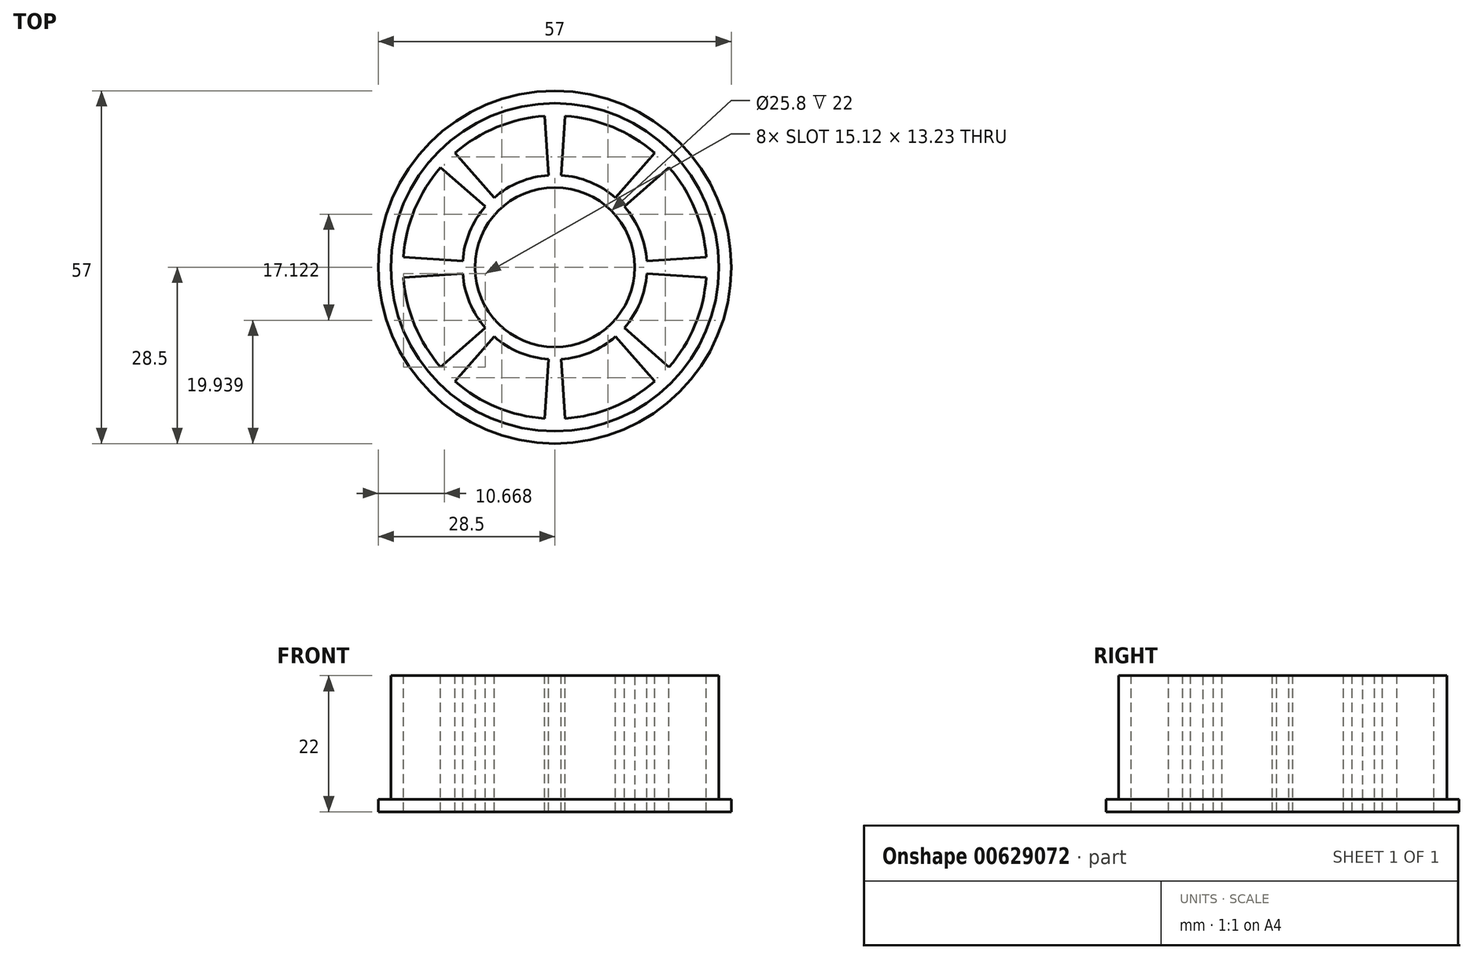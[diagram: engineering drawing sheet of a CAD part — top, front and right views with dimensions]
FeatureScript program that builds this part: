
annotation { "Feature Type Name" : "Feature", "Feature Type Description" : "" }
export const myFeature = defineFeature(function(context is Context, id is Id, definition is map)
    precondition{}
    {
        {
            var Q0;
            Q0=qCreatedBy(makeId("Top.planeOp"),FACE);
            var sketch = newSketch(context, id + "F0", { "sketchPlane" : qUnion([Q0])});
            skCircle(sketch, "E0", {"center": v(0, 0) * mm, "radius": 28.5 * mm});
            skCircle(sketch, "E1", {"center": v(0, 0) * mm, "radius": 26.5 * mm});
            skCircle(sketch, "E2", {"center": v(0, 0) * mm, "radius": 12.9 * mm});
            skSolve(sketch);
        }
        {
            var Q0;
            Q0=makeQuery(id+"F0.imprint","IMPRINT",FACE,{"disambiguationData":[TD([[makeQuery(id+"F0.imprint","IMPRINT",EDGE,{"derivedFrom":sQuery(id+"F0.wireOp",EDGE,"E1")}),1.0]])]});
            extrude(context, id + "F1", {"entities" : qUnion([Q0]), "depth" : 22 * mm, "offsetDistance" : 25 * mm});
        }
        {
            var Q0;
            Q0=makeQuery(id+"F0.imprint","IMPRINT",FACE,{"disambiguationData":[TD([[makeQuery(id+"F0.imprint","IMPRINT",EDGE,{"derivedFrom":sQuery(id+"F0.wireOp",EDGE,"E0")}),1.0]])]});
            extrude(context, id + "F2", {"entities" : qUnion([Q0]), "operationType" : NewBodyOperationType.ADD, "depth" : 2 * mm, "offsetDistance" : 25 * mm});
        }
        {
            var Q0;
            Q0=makeQuery(id+"F1.opExtrude","CAP_FACE",FACE,{"disambiguationData":[OSD([sQuery(id+"F0.wireOp",EDGE,"E1"),sQuery(id+"F0.wireOp",EDGE,"E2")])],"isStart":false});
            var sketch = newSketch(context, id + "F3", { "sketchPlane" : qUnion([Q0])});
            skLineSegment(sketch, "E3", {"start": v(16.12, -18.45) * mm, "end": v(9.8, -11.22) * mm});
            skLineSegment(sketch, "E4", {"start": v(1.64, -24.44) * mm, "end": v(1, -14.87) * mm});
            skArc(sketch, "E5", {"start": v(1, -14.87) * mm, "mid": v(5.7, -13.77) * mm, "end": v(9.8, -11.22) * mm});
            skArc(sketch, "E6", {"start": v(1.64, -24.44) * mm, "mid": v(9.38, -22.64) * mm, "end": v(16.12, -18.45) * mm});
            skLineSegment(sketch, "E7", {"start": v(18.74, -18.74) * mm, "end": v(0, 0) * mm, "construction": true});
            skSolve(sketch);
        }
        {
            var Q0;
            Q0 = qSketchRegion(id + "F3", true);
            var Q1;
            {var subQ0=sQuery(id+"F0.wireOp",EDGE,"E1");Q1=makeQuery(id+"F2.boolean.opBoolean","MERGE",FACE,{"derivedFrom":[makeQuery(id+"F1.opExtrude","CAP_FACE",FACE,{"disambiguationData":[OSD([subQ0,sQuery(id+"F0.wireOp",EDGE,"E2")])],"isStart":true}),makeQuery(id+"F2.opExtrude","CAP_FACE",FACE,{"disambiguationData":[OSD([sQuery(id+"F0.wireOp",EDGE,"E0"),subQ0])],"isStart":true})]});}
            extrude(context, id + "F4", {"entities" : qUnion([Q0]), "endBound" : BoundingType.UP_TO_SURFACE, "oppositeDirection" : true, "depth" : 25 * mm, "endBoundEntityFace" : qUnion([Q1]), "offsetDistance" : 25 * mm});
        }
        {
            var Q0;
            Q0=makeQuery(id+"F4.opExtrude","SWEPT_BODY",BODY,{"disambiguationData":[OSD([sQuery(id+"F3.wireOp",EDGE,"E3"),sQuery(id+"F3.wireOp",EDGE,"E4"),sQuery(id+"F3.wireOp",EDGE,"E5"),sQuery(id+"F3.wireOp",EDGE,"E6")])]});
            var Q1;
            Q1=makeQuery(id+"F1.opExtrude","SWEPT_FACE",FACE,{"disambiguationData":[OSD([sQuery(id+"F0.wireOp",EDGE,"E2")])]});
            circularPattern(context, id + "F5", {"entities" : qUnion([Q0]), "axis" : qUnion([Q1]), "angle" : 360 * degree, "instanceCount" : 8, "equalSpace" : true});
        }
        {
            var Q0;
            Q0=makeQuery(id+"F4.opExtrude","SWEPT_BODY",BODY,{"disambiguationData":[OSD([sQuery(id+"F3.wireOp",EDGE,"E3"),sQuery(id+"F3.wireOp",EDGE,"E4"),sQuery(id+"F3.wireOp",EDGE,"E5"),sQuery(id+"F3.wireOp",EDGE,"E6")])]});
            var Q1;
            Q1=makeQuery(id+"F5.opPattern","COPY",BODY,{"derivedFrom":makeQuery(id+"F4.opExtrude","SWEPT_BODY",BODY,{"disambiguationData":[OSD([sQuery(id+"F3.wireOp",EDGE,"E3"),sQuery(id+"F3.wireOp",EDGE,"E4"),sQuery(id+"F3.wireOp",EDGE,"E5"),sQuery(id+"F3.wireOp",EDGE,"E6")])]}),"instanceName":"7"});
            var Q2;
            Q2=makeQuery(id+"F5.opPattern","COPY",BODY,{"derivedFrom":makeQuery(id+"F4.opExtrude","SWEPT_BODY",BODY,{"disambiguationData":[OSD([sQuery(id+"F3.wireOp",EDGE,"E3"),sQuery(id+"F3.wireOp",EDGE,"E4"),sQuery(id+"F3.wireOp",EDGE,"E5"),sQuery(id+"F3.wireOp",EDGE,"E6")])]}),"instanceName":"6"});
            var Q3;
            Q3=makeQuery(id+"F5.opPattern","COPY",BODY,{"derivedFrom":makeQuery(id+"F4.opExtrude","SWEPT_BODY",BODY,{"disambiguationData":[OSD([sQuery(id+"F3.wireOp",EDGE,"E3"),sQuery(id+"F3.wireOp",EDGE,"E4"),sQuery(id+"F3.wireOp",EDGE,"E5"),sQuery(id+"F3.wireOp",EDGE,"E6")])]}),"instanceName":"5"});
            var Q4;
            Q4=makeQuery(id+"F5.opPattern","COPY",BODY,{"derivedFrom":makeQuery(id+"F4.opExtrude","SWEPT_BODY",BODY,{"disambiguationData":[OSD([sQuery(id+"F3.wireOp",EDGE,"E3"),sQuery(id+"F3.wireOp",EDGE,"E4"),sQuery(id+"F3.wireOp",EDGE,"E5"),sQuery(id+"F3.wireOp",EDGE,"E6")])]}),"instanceName":"4"});
            var Q5;
            Q5=makeQuery(id+"F5.opPattern","COPY",BODY,{"derivedFrom":makeQuery(id+"F4.opExtrude","SWEPT_BODY",BODY,{"disambiguationData":[OSD([sQuery(id+"F3.wireOp",EDGE,"E3"),sQuery(id+"F3.wireOp",EDGE,"E4"),sQuery(id+"F3.wireOp",EDGE,"E5"),sQuery(id+"F3.wireOp",EDGE,"E6")])]}),"instanceName":"3"});
            var Q6;
            Q6=makeQuery(id+"F5.opPattern","COPY",BODY,{"derivedFrom":makeQuery(id+"F4.opExtrude","SWEPT_BODY",BODY,{"disambiguationData":[OSD([sQuery(id+"F3.wireOp",EDGE,"E3"),sQuery(id+"F3.wireOp",EDGE,"E4"),sQuery(id+"F3.wireOp",EDGE,"E5"),sQuery(id+"F3.wireOp",EDGE,"E6")])]}),"instanceName":"2"});
            var Q7;
            Q7=makeQuery(id+"F5.opPattern","COPY",BODY,{"derivedFrom":makeQuery(id+"F4.opExtrude","SWEPT_BODY",BODY,{"disambiguationData":[OSD([sQuery(id+"F3.wireOp",EDGE,"E3"),sQuery(id+"F3.wireOp",EDGE,"E4"),sQuery(id+"F3.wireOp",EDGE,"E5"),sQuery(id+"F3.wireOp",EDGE,"E6")])]}),"instanceName":"1"});
            var Q8;
            Q8=makeQuery(id+"F1.opExtrude","SWEPT_BODY",BODY,{"disambiguationData":[OSD([sQuery(id+"F0.wireOp",EDGE,"E1"),sQuery(id+"F0.wireOp",EDGE,"E2")])]});
            booleanBodies(context, id + "F6", {"operationType" : BooleanOperationType.SUBTRACTION, "tools" : qUnion([Q0, Q1, Q2, Q3, Q4, Q5, Q6, Q7]), "targets" : qUnion([Q8])});
        }
    });
